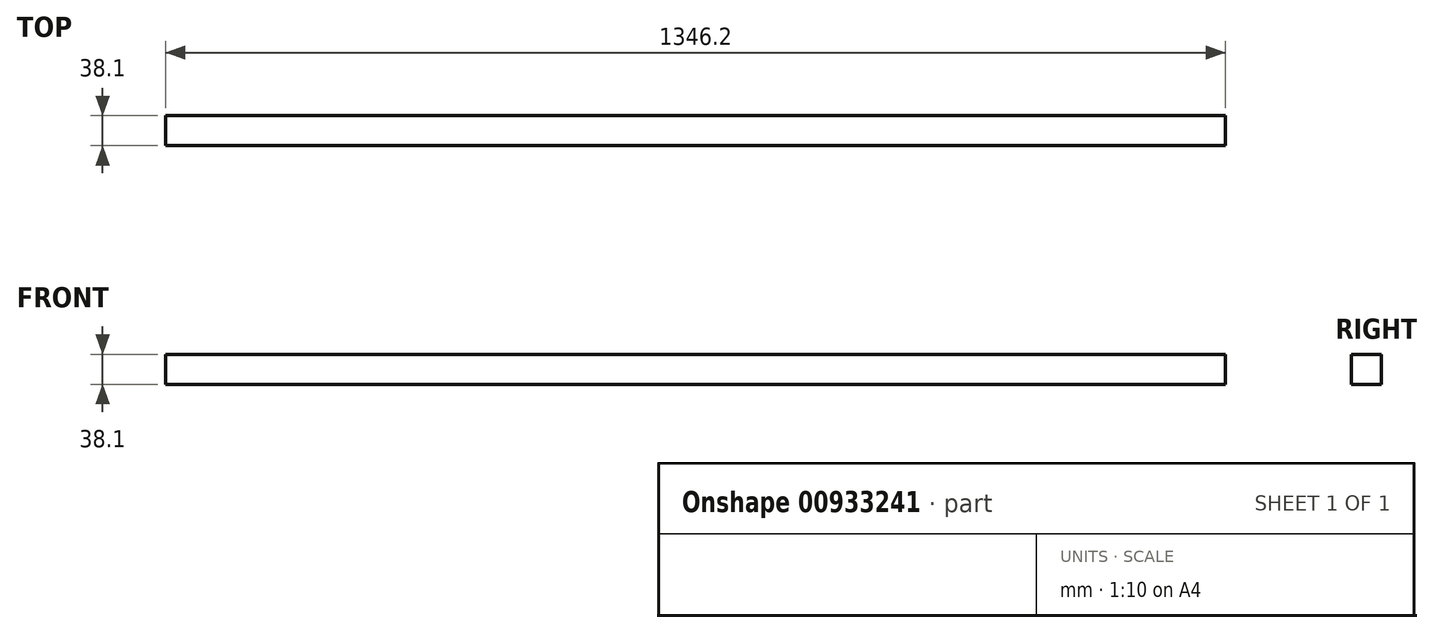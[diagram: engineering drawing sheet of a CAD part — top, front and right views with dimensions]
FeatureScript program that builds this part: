
annotation { "Feature Type Name" : "Feature", "Feature Type Description" : "" }
export const myFeature = defineFeature(function(context is Context, id is Id, definition is map)
    precondition{}
    {
        {
            var Q0;
            Q0=qCreatedBy(makeId("Front.planeOp"),FACE);
            var sketch = newSketch(context, id + "F0", { "sketchPlane" : qUnion([Q0])});
            skLineSegment(sketch, "E0.bottom", {"start": v(-673.1, 19.05) * mm, "end": v(673.1, 19.05) * mm});
            skLineSegment(sketch, "E0.top", {"start": v(-673.1, -19.05) * mm, "end": v(673.1, -19.05) * mm});
            skLineSegment(sketch, "E0.left", {"start": v(-673.1, 19.05) * mm, "end": v(-673.1, -19.05) * mm});
            skLineSegment(sketch, "E0.right", {"start": v(673.1, 19.05) * mm, "end": v(673.1, -19.05) * mm});
            skPoint(sketch, "E0.middle", {"position": v(0, 0) * mm});
            skSolve(sketch);
        }
        {
            var Q0;
            Q0=makeQuery(id+"F0.imprint","IMPRINT",FACE,{"disambiguationData":[TD([[makeQuery(id+"F0.imprint","IMPRINT",EDGE,{"derivedFrom":sQuery(id+"F0.wireOp",EDGE,"E0.bottom")}),-1.0]])]});
            extrude(context, id + "F1", {"entities" : qUnion([Q0]), "depth" : 38.1 * mm, "offsetDistance" : 25.4 * mm});
        }
    });
